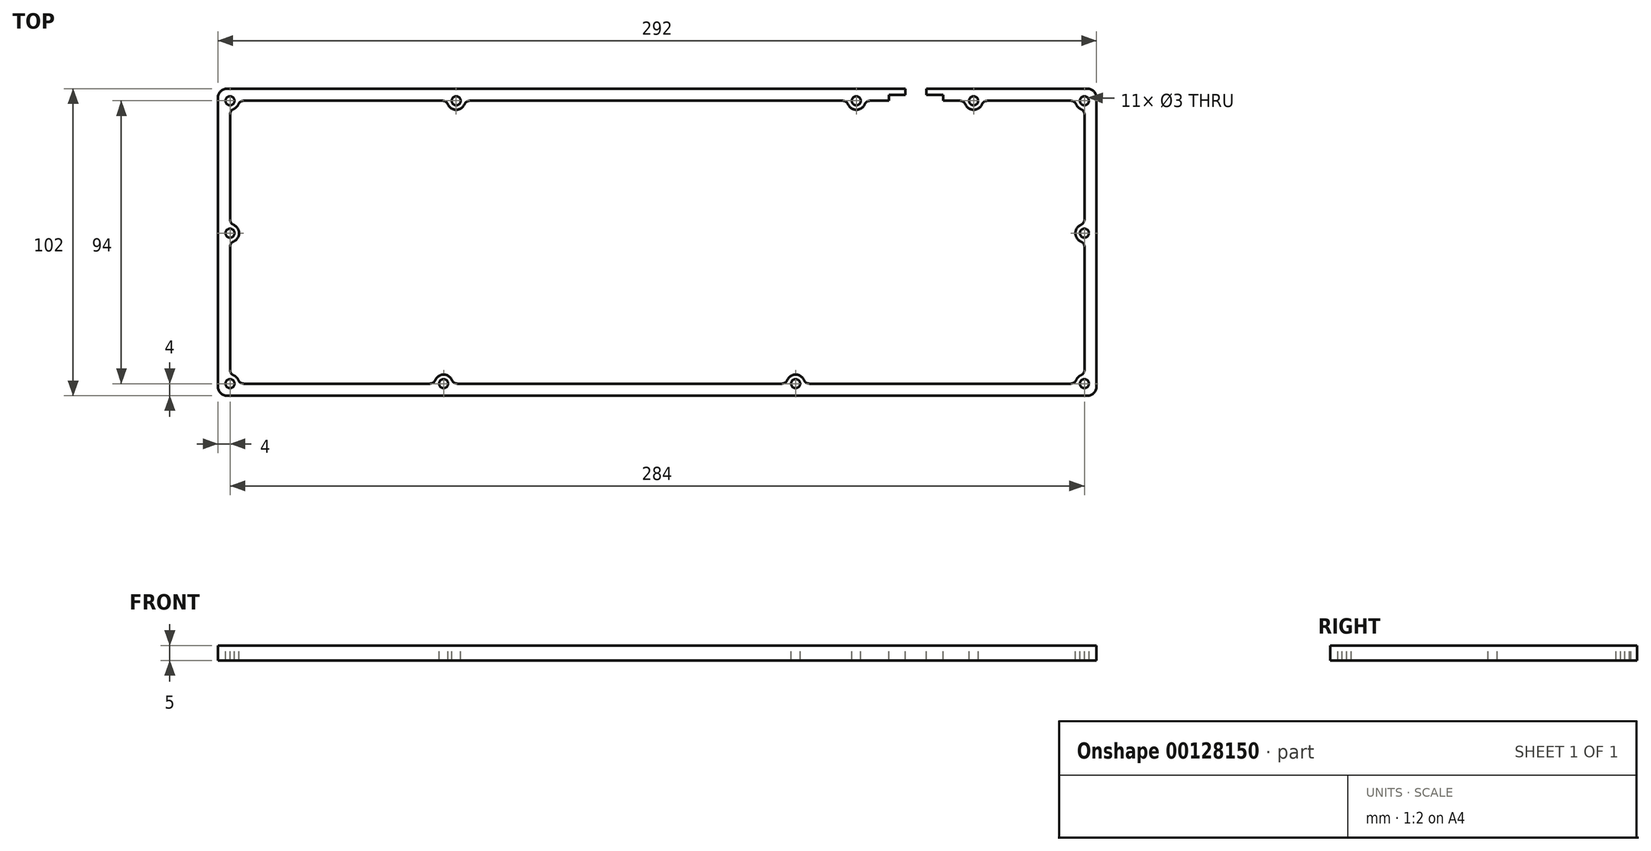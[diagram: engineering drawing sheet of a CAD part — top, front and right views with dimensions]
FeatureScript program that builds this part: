
annotation { "Feature Type Name" : "Feature", "Feature Type Description" : "" }
export const myFeature = defineFeature(function(context is Context, id is Id, definition is map)
    precondition{}
    {
        {
            var Q0;
            Q0=qCreatedBy(makeId("Top.planeOp"),FACE);
            var sketch = newSketch(context, id + "F0", { "sketchPlane" : qUnion([Q0])});
            skLineSegment(sketch, "E0.bottom", {"start": v(143, 51) * mm, "end": v(-143, 51) * mm});
            skLineSegment(sketch, "E0.top", {"start": v(143, -51) * mm, "end": v(-143, -51) * mm});
            skLineSegment(sketch, "E0.left", {"start": v(146, 48) * mm, "end": v(146, -48) * mm});
            skLineSegment(sketch, "E0.right", {"start": v(-146, 48) * mm, "end": v(-146, -48) * mm});
            skPoint(sketch, "E1.visualSharp", {"position": v(-146, 51) * mm});
            skArc(sketch, "E1.filletArc", {"start": v(-143, 51) * mm, "mid": v(-145.12, 50.12) * mm, "end": v(-146, 48) * mm});
            skPoint(sketch, "E2.visualSharp", {"position": v(-146, -51) * mm});
            skArc(sketch, "E2.filletArc", {"start": v(-146, -48) * mm, "mid": v(-145.12, -50.12) * mm, "end": v(-143, -51) * mm});
            skPoint(sketch, "E3.visualSharp", {"position": v(146, -51) * mm});
            skArc(sketch, "E3.filletArc", {"start": v(143, -51) * mm, "mid": v(145.12, -50.12) * mm, "end": v(146, -48) * mm});
            skArc(sketch, "E4.filletArc", {"start": v(146, 48) * mm, "mid": v(145.12, 50.12) * mm, "end": v(143, 51) * mm});
            skSolve(sketch);
        }
        {
            var Q0;
            Q0=qSketchRegion(id+"F0",true);
            extrude(context, id + "F1", {"entities" : qUnion([Q0]), "depth" : 5 * mm});
        }
        {
            var Q0;
            Q0=makeQuery(id+"F1.opExtrude","CAP_FACE",FACE,{"disambiguationData":[OSD([sQuery(id+"F0.wireOp",EDGE,"b1609128-1e4d-4f99-a9c0-d1eb6efb653b"),sQuery(id+"F0.wireOp",EDGE,"f4566b4f-cb64-43fb-b69e-2d4997d02e9e"),sQuery(id+"F0.wireOp",EDGE,"c58de4d6-b1a3-4d1c-92d8-0e596c6fe70e"),sQuery(id+"F0.wireOp",EDGE,"5249d06f-5fa9-4bc2-861d-4cda040d6d12"),sQuery(id+"F0.wireOp",EDGE,"a85e44d5-a424-4784-8d57-3f87bcd3cb1f"),sQuery(id+"F0.wireOp",EDGE,"26f2ad72-3e01-41bb-a775-2f8cfdfabe7d"),sQuery(id+"F0.wireOp",EDGE,"58a866ff-a5cd-410d-a599-dedaca65d45f"),sQuery(id+"F0.wireOp",EDGE,"ffbf0b70-5c72-4423-8b02-8f3d0a3b2328"),sQuery(id+"F0.wireOp",EDGE,"7f67b6f4-1288-461f-aa79-609977e3f21a"),sQuery(id+"F0.wireOp",EDGE,"55541f8a-b999-41dc-948e-6a4feb6e2708"),sQuery(id+"F0.wireOp",EDGE,"6f56692b-9edc-44ed-85e6-53072711c858"),sQuery(id+"F0.wireOp",EDGE,"d64ee7ec-02fb-4461-892d-8620c137c8be"),sQuery(id+"F0.wireOp",EDGE,"a331adab-5858-4e06-9c1d-1ebd579e2d6c"),sQuery(id+"F0.wireOp",EDGE,"872b245d-4d85-40be-bc62-1036af002ab7"),sQuery(id+"F0.wireOp",EDGE,"5f5c10bb-96b1-40b4-bf40-71e8b90fd5b4"),sQuery(id+"F0.wireOp",EDGE,"070c8fee-8489-4fd5-82cc-431f9b446bf5"),sQuery(id+"F0.wireOp",EDGE,"0514bdef-a2e6-47cc-91cb-2d3d024f583d"),sQuery(id+"F0.wireOp",EDGE,"38748b5d-75be-4e41-86c7-7b4e33a636ad"),sQuery(id+"F0.wireOp",EDGE,"ef5fee99-fa31-4ebf-9718-ae6e1dd8c854"),sQuery(id+"F0.wireOp",EDGE,"33aefef2-9a3a-4597-9de5-3f6917e2cb92"),sQuery(id+"F0.wireOp",EDGE,"f576047e-5c30-44eb-8430-c6ba2e10f578"),sQuery(id+"F0.wireOp",EDGE,"5237e12e-b54f-4000-b0ec-e2a188ff4113"),sQuery(id+"F0.wireOp",EDGE,"39a89d85-1c88-4538-9ca2-57a00aa53215"),sQuery(id+"F0.wireOp",EDGE,"1d3d1f3f-65d5-432a-a24c-25425600a27e"),sQuery(id+"F0.wireOp",EDGE,"65133dcd-ba31-495c-9030-11ebdab85244"),sQuery(id+"F0.wireOp",EDGE,"59442c7d-f29c-40c5-8460-04e0c5612805"),sQuery(id+"F0.wireOp",EDGE,"7c508e6d-ace5-438d-ae87-594742bffb03"),sQuery(id+"F0.wireOp",EDGE,"96358abd-ade1-4970-8e96-f48957cb49a9"),sQuery(id+"F0.wireOp",EDGE,"beaf586f-d415-4bcd-bc2c-fe17f6c56d29"),sQuery(id+"F0.wireOp",EDGE,"0b1e909e-c7ab-4355-90a4-b9d381122b20"),sQuery(id+"F0.wireOp",EDGE,"07e25036-969a-447a-8387-7472eab81c53"),sQuery(id+"F0.wireOp",EDGE,"4ac198d4-a843-4e16-ab13-53b4b61c7ec9"),sQuery(id+"F0.wireOp",EDGE,"5899e998-bb7d-4984-919d-5380da3ef46d"),sQuery(id+"F0.wireOp",EDGE,"85bf5025-0c0a-493d-8fd5-15a1002b9e1f"),sQuery(id+"F0.wireOp",EDGE,"433a8b32-5078-4fa2-bccb-dd94966a19e2"),sQuery(id+"F0.wireOp",EDGE,"ca2aed50-1aac-4a88-af60-10e4d26c56ce"),sQuery(id+"F0.wireOp",EDGE,"ad785477-14a5-48c7-ba58-707c46f4f765"),sQuery(id+"F0.wireOp",EDGE,"7e877f2a-03cb-4247-a0d1-3f1f17d45f2e"),sQuery(id+"F0.wireOp",EDGE,"5549e225-b8b0-41a5-a1f6-3a747b09e555"),sQuery(id+"F0.wireOp",EDGE,"7757f798-a692-4454-bd86-5a4d4f9a0c34"),sQuery(id+"F0.wireOp",EDGE,"3016f92a-8452-4434-919c-4a7fc7338035"),sQuery(id+"F0.wireOp",EDGE,"898612aa-0cec-428b-94af-f86252429d12"),sQuery(id+"F0.wireOp",EDGE,"a17dd576-292f-4e6b-9663-d9180f696670"),sQuery(id+"F0.wireOp",EDGE,"cbfd38bd-20b5-4d44-be8c-a17f12e052e0"),sQuery(id+"F0.wireOp",EDGE,"70ab0708-ffdb-4529-bf9e-4018cae3591c"),sQuery(id+"F0.wireOp",EDGE,"f406bcac-c7ef-481d-8174-8bc63e706a56"),sQuery(id+"F0.wireOp",EDGE,"dc331ac5-7670-45e9-89c7-03810e187fe8"),sQuery(id+"F0.wireOp",EDGE,"b3191053-ceed-4c24-bda0-5a50d567a071"),sQuery(id+"F0.wireOp",EDGE,"e110f5b5-6a02-4a34-82cf-196097ccbeb4"),sQuery(id+"F0.wireOp",EDGE,"2b5f7b66-3d2f-406f-a6d7-9a85497eda15"),sQuery(id+"F0.wireOp",EDGE,"76b1751e-cd68-4467-988c-686db3de7683"),sQuery(id+"F0.wireOp",EDGE,"16c5760e-34d5-4e50-8f9d-3caf3d151e1b"),sQuery(id+"F0.wireOp",EDGE,"d295ed9f-bfde-424d-aa21-20497ae6f13c"),sQuery(id+"F0.wireOp",EDGE,"ec12ba42-fae9-4e41-9ad7-bf38757b17f0"),sQuery(id+"F0.wireOp",EDGE,"7436cc0e-6ec4-46fe-a53e-8bd212bcf723"),sQuery(id+"F0.wireOp",EDGE,"0cedb4c9-6a6c-43c2-9996-506471cd3255"),sQuery(id+"F0.wireOp",EDGE,"ec54193d-d4cb-4b1f-86fc-2851957baaba"),sQuery(id+"F0.wireOp",EDGE,"4488f506-9ef2-4267-a6cf-a7b00e78e843"),sQuery(id+"F0.wireOp",EDGE,"372820ab-3034-42cd-b4e6-65ef871f9c40"),sQuery(id+"F0.wireOp",EDGE,"6573e008-ca1a-4dee-91fb-cecced364ef1"),sQuery(id+"F0.wireOp",EDGE,"0ea65bf7-9227-4dbe-9352-82978ca5b32e"),sQuery(id+"F0.wireOp",EDGE,"b1bb12b1-79df-4f2c-a40f-21d0aa567c24"),sQuery(id+"F0.wireOp",EDGE,"0c1536de-d6b0-46e4-9ba7-2841298be202"),sQuery(id+"F0.wireOp",EDGE,"207e1af1-11f0-4a44-9182-2a9f56c0d657"),sQuery(id+"F0.wireOp",EDGE,"27c13fe8-c982-4180-82e1-206dc62b37cb"),sQuery(id+"F0.wireOp",EDGE,"df3f2611-b4d2-4e5e-a9a9-9197ed178f10"),sQuery(id+"F0.wireOp",EDGE,"67ca35e5-e03d-4edf-9133-55c0f28c00dd"),sQuery(id+"F0.wireOp",EDGE,"211b09a9-55cd-462d-ac42-8101b668ed7f"),sQuery(id+"F0.wireOp",EDGE,"3790da84-eb6b-418a-b30a-773cb8711b72"),sQuery(id+"F0.wireOp",EDGE,"8ad775da-4dcc-4f57-b984-0bd12b45c958"),sQuery(id+"F0.wireOp",EDGE,"46f09f23-81b2-4bbc-9572-84064063ea46"),sQuery(id+"F0.wireOp",EDGE,"375117c6-4bbc-4c16-b11f-bde5a02c8ddd"),sQuery(id+"F0.wireOp",EDGE,"edf3fd68-21bd-4dda-b02f-30e2386ebe8c"),sQuery(id+"F0.wireOp",EDGE,"e9b376d0-4e66-4361-894a-f7f99b0a4dba"),sQuery(id+"F0.wireOp",EDGE,"7deef6e9-a95f-4fef-90d6-14df86437aaf"),sQuery(id+"F0.wireOp",EDGE,"3a2c3b9f-72e5-46fb-b22f-c3b3668238e3"),sQuery(id+"F0.wireOp",EDGE,"ef61160d-285f-4999-b3d1-3ad131a5c696"),sQuery(id+"F0.wireOp",EDGE,"5e485a8d-fc2c-447f-9fb7-2a8e8f7db1b8"),sQuery(id+"F0.wireOp",EDGE,"be4b73c1-2188-4d56-b092-b0e9aa332c99"),sQuery(id+"F0.wireOp",EDGE,"7886a41d-8e50-4074-9c4a-38b5df8d299c"),sQuery(id+"F0.wireOp",EDGE,"4e7a6acf-1550-41f7-a348-87a73df4ade2"),sQuery(id+"F0.wireOp",EDGE,"3075fc72-2a9a-4c54-a333-3b9aff6871ba"),sQuery(id+"F0.wireOp",EDGE,"1b470988-ea39-4ef3-b94f-c351ab6970c0"),sQuery(id+"F0.wireOp",EDGE,"d5d0fb32-3312-47e0-b08e-500f4e3a8d6f"),sQuery(id+"F0.wireOp",EDGE,"c95a7a57-a701-41e8-a435-0717771ea27e"),sQuery(id+"F0.wireOp",EDGE,"72f5413f-f806-4961-a1f2-17e8c49a2dbe"),sQuery(id+"F0.wireOp",EDGE,"12295bb0-ec03-4baf-b844-216b01d10c7f"),sQuery(id+"F0.wireOp",EDGE,"ea74abaf-c7a4-4655-a14d-8def43b58c3b"),sQuery(id+"F0.wireOp",EDGE,"fc38e52a-d66c-41f3-a18f-2ab74fc9a3aa"),sQuery(id+"F0.wireOp",EDGE,"b9a872e7-607d-4140-9fac-37e865748f2f"),sQuery(id+"F0.wireOp",EDGE,"469ab4fc-23a3-4a44-8d10-edb1ebb05813"),sQuery(id+"F0.wireOp",EDGE,"6c8f3efd-a16e-4969-a36d-9367de4a04a8"),sQuery(id+"F0.wireOp",EDGE,"d914cece-980e-4aa7-9a19-217e5638b189"),sQuery(id+"F0.wireOp",EDGE,"0d8dcd5d-387b-402a-9c60-ffcbd0bb72cc"),sQuery(id+"F0.wireOp",EDGE,"8cf55217-a1b6-4c1c-9f03-72966d881f0b"),sQuery(id+"F0.wireOp",EDGE,"4053d66f-c8cf-4424-b222-ee203ee23c1e"),sQuery(id+"F0.wireOp",EDGE,"87d9ca37-d664-469b-a4c7-7af1bd52c0ff"),sQuery(id+"F0.wireOp",EDGE,"c0a5d230-8ae8-4271-ac44-5db517de8359"),sQuery(id+"F0.wireOp",EDGE,"1c324c12-bb8f-4aad-bd93-a065141bcc31"),sQuery(id+"F0.wireOp",EDGE,"5157ba3e-39b2-42a3-aeba-34e1f65bc982"),sQuery(id+"F0.wireOp",EDGE,"37ae300f-3520-4053-852e-9cb6712c105c"),sQuery(id+"F0.wireOp",EDGE,"e56d4f24-566a-4093-9c1d-03fa3ce6c3fd"),sQuery(id+"F0.wireOp",EDGE,"c14c5ada-49ad-40e8-9107-312975a1c3f7"),sQuery(id+"F0.wireOp",EDGE,"09f918fb-f6ba-4f35-826c-9be1aaa1e634"),sQuery(id+"F0.wireOp",EDGE,"1a04a7b3-ebb9-45f2-aa82-77a2838be510"),sQuery(id+"F0.wireOp",EDGE,"8b1de847-c452-41c5-811c-5ab6a2f757b0"),sQuery(id+"F0.wireOp",EDGE,"07133ebf-dc20-4f31-a97c-dbe7588edc2e"),sQuery(id+"F0.wireOp",EDGE,"82b11f7f-3426-4d96-a479-9e8199cbbcbe"),sQuery(id+"F0.wireOp",EDGE,"692c3182-390b-47c5-b81b-f7c9554c5188"),sQuery(id+"F0.wireOp",EDGE,"ec9cd909-a83d-4db2-80ed-a48da1c01f2a"),sQuery(id+"F0.wireOp",EDGE,"8999d2ee-b3fd-40a3-91db-70ba8707524c"),sQuery(id+"F0.wireOp",EDGE,"877071da-4e0e-44ee-80f9-18e6a312fe40"),sQuery(id+"F0.wireOp",EDGE,"310de26f-e1f4-4f76-a7a2-31cd6309eb9f"),sQuery(id+"F0.wireOp",EDGE,"ad3c8448-077b-42fa-b66f-cb204dd4b24b"),sQuery(id+"F0.wireOp",EDGE,"dc182899-f22f-43ca-bb7a-d9cff2bb14a0"),sQuery(id+"F0.wireOp",EDGE,"65f270fc-c84c-425a-8765-446292cb4d3e"),sQuery(id+"F0.wireOp",EDGE,"c2b09f90-88b6-4d72-8a72-16f5e25146eb"),sQuery(id+"F0.wireOp",EDGE,"c2295a2a-ded6-4c6f-a2aa-a895bf3941d7"),sQuery(id+"F0.wireOp",EDGE,"c37eb4cb-c588-4c6c-82ac-1d42e178e50a"),sQuery(id+"F0.wireOp",EDGE,"c6fafc2d-4fcb-4607-9bd2-8190c812e452"),sQuery(id+"F0.wireOp",EDGE,"9417043a-912b-430b-98cd-4ce252294d8a"),sQuery(id+"F0.wireOp",EDGE,"25218a79-4e2b-4d76-88a5-5a80dd25db46"),sQuery(id+"F0.wireOp",EDGE,"52fe2f22-f5c3-47de-b85b-7071680885e1"),sQuery(id+"F0.wireOp",EDGE,"8db425a6-9809-493b-a625-842b3707d4f8"),sQuery(id+"F0.wireOp",EDGE,"108efb8e-72e4-46dc-b29e-3530763ab2cb"),sQuery(id+"F0.wireOp",EDGE,"37e6c475-f92b-460d-bb35-4d3434045b59"),sQuery(id+"F0.wireOp",EDGE,"41b95ee3-14c1-4901-89de-568e1f007773"),sQuery(id+"F0.wireOp",EDGE,"01807cc5-b0aa-4840-a249-294bda683d07"),sQuery(id+"F0.wireOp",EDGE,"152e1f9d-8930-4523-a05f-674d844d7707"),sQuery(id+"F0.wireOp",EDGE,"5efd5115-699b-4425-b653-4cc125bcd7d7"),sQuery(id+"F0.wireOp",EDGE,"1cc39329-d833-44ea-a2f6-ea7c9f78653e"),sQuery(id+"F0.wireOp",EDGE,"0dca4560-2abc-4104-80a8-7adf0bc88beb"),sQuery(id+"F0.wireOp",EDGE,"6916323c-6478-4019-a811-1e709e75c72c"),sQuery(id+"F0.wireOp",EDGE,"2451c855-d06f-4170-a402-bb45c563284a"),sQuery(id+"F0.wireOp",EDGE,"8586e523-ca72-4acf-a6f5-917adcdadd36"),sQuery(id+"F0.wireOp",EDGE,"930f09bf-785d-44d0-a635-5104e1f2550d"),sQuery(id+"F0.wireOp",EDGE,"c441b449-73cf-46cf-ad09-9110f26cec35"),sQuery(id+"F0.wireOp",EDGE,"60176a13-c84b-409f-9b5c-2d317961481d"),sQuery(id+"F0.wireOp",EDGE,"fc777e31-b308-4b5e-985b-35cb478bdecb"),sQuery(id+"F0.wireOp",EDGE,"e88cf7bc-e46a-4de7-95e0-dad1476bcc0c"),sQuery(id+"F0.wireOp",EDGE,"96c8cf9e-4ec9-44d1-ad91-7186c6f1f209"),sQuery(id+"F0.wireOp",EDGE,"658329ac-6692-4e40-9ef8-a494bcb0f754"),sQuery(id+"F0.wireOp",EDGE,"d67bae1f-3ffd-4beb-8cc6-29e61c8b342c"),sQuery(id+"F0.wireOp",EDGE,"dbf715f9-25b6-4774-be77-851613eb5e25"),sQuery(id+"F0.wireOp",EDGE,"d8d12f8c-32ed-4466-a5bc-cbc1cfba4feb"),sQuery(id+"F0.wireOp",EDGE,"4beba3b0-c51b-4a43-948d-e7233947d5dc"),sQuery(id+"F0.wireOp",EDGE,"fcfcb946-a851-45fe-a21c-e3f885e48000"),sQuery(id+"F0.wireOp",EDGE,"4d44fab2-dba1-4fbc-848d-77cfe8fac08b"),sQuery(id+"F0.wireOp",EDGE,"5776a788-e3c3-4dac-aeb6-7777a672858e"),sQuery(id+"F0.wireOp",EDGE,"cedf499e-2994-4c9b-b766-b127bb67c415"),sQuery(id+"F0.wireOp",EDGE,"0a2e2db6-b390-46fd-b74c-53757edf0af6"),sQuery(id+"F0.wireOp",EDGE,"4ce94d68-acc0-4cfe-bd55-ec03fe200a5b"),sQuery(id+"F0.wireOp",EDGE,"e0c07793-b957-4333-96dc-a294f1e2ceb0"),sQuery(id+"F0.wireOp",EDGE,"41979a11-f1a0-4749-a17a-603b7864cc01"),sQuery(id+"F0.wireOp",EDGE,"aa3ca26f-036c-439d-b566-5430048ebdf9"),sQuery(id+"F0.wireOp",EDGE,"249b810b-8968-482f-8bbc-e4399ea1180f"),sQuery(id+"F0.wireOp",EDGE,"3f1de34e-7a13-4160-8f1e-59d99b5a4c3a"),sQuery(id+"F0.wireOp",EDGE,"f0e1049c-435a-4f02-948e-5f98f668222f"),sQuery(id+"F0.wireOp",EDGE,"dceacdf6-e703-4809-b70b-d17cfe04b7d7"),sQuery(id+"F0.wireOp",EDGE,"bdd4c6ec-239a-424d-8041-67786f5d4ce7"),sQuery(id+"F0.wireOp",EDGE,"44e7c303-723b-4c42-a54a-8f557ff9a9f6"),sQuery(id+"F0.wireOp",EDGE,"e59f6ee7-3ba8-4e2b-b5d6-6e605825de7d"),sQuery(id+"F0.wireOp",EDGE,"3867d971-9346-4093-a9b2-274161278cdc"),sQuery(id+"F0.wireOp",EDGE,"d52ba1ae-d7a3-467c-9b67-1ae8c09bf28e"),sQuery(id+"F0.wireOp",EDGE,"1800a961-f957-4766-bec1-88f23ee5c048"),sQuery(id+"F0.wireOp",EDGE,"944022d4-31d1-4345-9843-0181748df1e1"),sQuery(id+"F0.wireOp",EDGE,"56ca7d79-5fc4-42fd-843a-33c232b6b3c3"),sQuery(id+"F0.wireOp",EDGE,"098c2286-8095-4fed-8dd0-5a8dec876cb3"),sQuery(id+"F0.wireOp",EDGE,"2ad36734-b040-4264-b8f6-ee2da5387eb9"),sQuery(id+"F0.wireOp",EDGE,"ccc487cc-2c29-4e42-a366-3ba57780b9a2"),sQuery(id+"F0.wireOp",EDGE,"7b328234-d38a-4842-b15d-1fbe1fd70208"),sQuery(id+"F0.wireOp",EDGE,"3732f762-4107-4d06-83e4-c8630a2c37fb"),sQuery(id+"F0.wireOp",EDGE,"8b64106c-834e-4e21-a7c0-f3940f540fb2"),sQuery(id+"F0.wireOp",EDGE,"6e7361da-996f-46b3-a434-00db9b4c9c9f"),sQuery(id+"F0.wireOp",EDGE,"b0b43ae6-5ac0-41e1-a04e-e485c33c99f8"),sQuery(id+"F0.wireOp",EDGE,"db5e65e6-5182-4048-9572-11a43cb11c51"),sQuery(id+"F0.wireOp",EDGE,"26e7e85a-b403-48fa-8c29-07448647ad8f"),sQuery(id+"F0.wireOp",EDGE,"515b21e0-8220-4d96-96a0-4c14be87b64b"),sQuery(id+"F0.wireOp",EDGE,"aa12bfdd-f8d8-4067-91a8-122e35d45f26"),sQuery(id+"F0.wireOp",EDGE,"9aa84255-1989-40c3-bf0d-31009647c77f"),sQuery(id+"F0.wireOp",EDGE,"aa9638c1-c68d-45f6-940c-d0f327c0fa45"),sQuery(id+"F0.wireOp",EDGE,"251b7c26-2c5b-48f1-8bde-e20a856a34ff"),sQuery(id+"F0.wireOp",EDGE,"18e7e5a9-24b2-485b-ab29-6ec4d7284516"),sQuery(id+"F0.wireOp",EDGE,"f4cd6263-1ac9-4123-a1aa-8b6f3d1fe724"),sQuery(id+"F0.wireOp",EDGE,"34207eab-8dad-445e-ac2c-5e7baad48e02"),sQuery(id+"F0.wireOp",EDGE,"d2cd9a5c-99c8-49cb-9122-6c3893475af4"),sQuery(id+"F0.wireOp",EDGE,"0ab99930-a22d-41a5-8d7a-f072e43d683d"),sQuery(id+"F0.wireOp",EDGE,"ba1f877b-ae2d-41b0-a78f-99f645971353"),sQuery(id+"F0.wireOp",EDGE,"7655611b-0d56-496a-9af6-17078dfc8983"),sQuery(id+"F0.wireOp",EDGE,"2217c71d-48f5-44f0-b6aa-e70c41dec14e"),sQuery(id+"F0.wireOp",EDGE,"2da62ed5-bda3-4005-8c82-b2de019464e8"),sQuery(id+"F0.wireOp",EDGE,"b9e5db85-9e65-4104-9569-ca807059eb4d"),sQuery(id+"F0.wireOp",EDGE,"e8855f58-9b24-4e18-bc1c-a0daeed810ba"),sQuery(id+"F0.wireOp",EDGE,"6c73f8f0-d719-4729-89df-4c554db3bf8c"),sQuery(id+"F0.wireOp",EDGE,"99502265-d697-4b9c-a12a-a7646a77523d"),sQuery(id+"F0.wireOp",EDGE,"5ad33bb7-7d8c-4f73-a2bd-749fa85a955e"),sQuery(id+"F0.wireOp",EDGE,"ffa3529a-edc2-4b05-9642-06e0e9a42b66"),sQuery(id+"F0.wireOp",EDGE,"221bf0c5-454d-44e2-b718-00ef1a2cf6b4"),sQuery(id+"F0.wireOp",EDGE,"2bf5e5ca-39b4-4044-8377-129965e258c5"),sQuery(id+"F0.wireOp",EDGE,"ba879806-eb56-4bd7-bf01-18ec1c857bc0"),sQuery(id+"F0.wireOp",EDGE,"64b71d1f-be08-4438-bafa-bb0b385583c3"),sQuery(id+"F0.wireOp",EDGE,"9a261f28-0ea3-4c64-a250-fe02b8de4198"),sQuery(id+"F0.wireOp",EDGE,"9c6a15b5-d89c-4f27-9035-4432c0c29f03"),sQuery(id+"F0.wireOp",EDGE,"39fc6f70-527d-491a-b3cc-87afca1fd921"),sQuery(id+"F0.wireOp",EDGE,"83ff7e70-d247-44e0-9e1a-45f528f1984e"),sQuery(id+"F0.wireOp",EDGE,"8c19abdc-fab5-49c6-a1e3-3ac5321561f2"),sQuery(id+"F0.wireOp",EDGE,"38f5175e-ca97-4091-a899-2fc862d9fcf7"),sQuery(id+"F0.wireOp",EDGE,"a6b59a2b-11a6-4381-9ec9-9e4786140b61"),sQuery(id+"F0.wireOp",EDGE,"a6aa3d57-10a3-484e-8f69-3d26024ead90"),sQuery(id+"F0.wireOp",EDGE,"cab9f132-7f02-4cf2-a837-44b314ab0f2d"),sQuery(id+"F0.wireOp",EDGE,"4d87c6e3-345b-4698-85be-4c1066c996ba"),sQuery(id+"F0.wireOp",EDGE,"100f6826-a35e-44dc-8f5e-91e6494c0734"),sQuery(id+"F0.wireOp",EDGE,"6b51b95a-e805-4a4c-b3ce-42549b1f7c4f"),sQuery(id+"F0.wireOp",EDGE,"4974438e-2757-4174-b66e-648bb066325b"),sQuery(id+"F0.wireOp",EDGE,"06557fa0-7690-4017-ac39-cec9dddb7ac3"),sQuery(id+"F0.wireOp",EDGE,"190d5702-5898-49b5-8b03-446313d35a85"),sQuery(id+"F0.wireOp",EDGE,"13d402cf-df92-4d9a-ac9d-1f67946c0a84"),sQuery(id+"F0.wireOp",EDGE,"2f2b7a4a-fe61-4bf2-9a19-afa51de3c721"),sQuery(id+"F0.wireOp",EDGE,"89631652-7db3-4c6b-99e7-db613ff7bbbb"),sQuery(id+"F0.wireOp",EDGE,"9bb81fc8-ca7b-4002-871d-2f89aed8432f"),sQuery(id+"F0.wireOp",EDGE,"a13c4922-8a72-4012-be87-7b5d4d768a52"),sQuery(id+"F0.wireOp",EDGE,"2badb0fd-de87-488b-8ff2-1cf5654be30e"),sQuery(id+"F0.wireOp",EDGE,"3885baab-ef1d-4d35-a85f-7a32c066c2bb"),sQuery(id+"F0.wireOp",EDGE,"5dec05d8-971c-49fe-8ee5-de689f2777ed"),sQuery(id+"F0.wireOp",EDGE,"4173ea56-7147-43d2-9c71-5769336bf9f5"),sQuery(id+"F0.wireOp",EDGE,"ac75d90e-cfd8-4d37-ba29-49a000d3f1ae"),sQuery(id+"F0.wireOp",EDGE,"98559af5-3831-4093-9a27-000fd7a0f36c"),sQuery(id+"F0.wireOp",EDGE,"e31d4e9e-ec26-4480-9e00-58e09570ae7e"),sQuery(id+"F0.wireOp",EDGE,"e82aada4-95ef-49cd-9523-bf5d0496c439"),sQuery(id+"F0.wireOp",EDGE,"21f6afce-f90f-4921-86bd-c08a04096671"),sQuery(id+"F0.wireOp",EDGE,"3c7f96f7-af1a-4bca-82d7-7f24edd57999"),sQuery(id+"F0.wireOp",EDGE,"9c442e46-f741-49c2-ae82-587b697e79f8"),sQuery(id+"F0.wireOp",EDGE,"f57068b1-2418-4c58-9872-b1a6e01bfd01"),sQuery(id+"F0.wireOp",EDGE,"aca98637-d3dc-411b-a35d-96c25150bc33"),sQuery(id+"F0.wireOp",EDGE,"d832a37b-e081-415c-bcce-cbaaf2c07a6e"),sQuery(id+"F0.wireOp",EDGE,"c9b6084d-535c-4eea-879b-8436754e0a02"),sQuery(id+"F0.wireOp",EDGE,"83c218aa-2010-4a7a-b09b-f6f7594d2848"),sQuery(id+"F0.wireOp",EDGE,"25d1440d-df07-499d-9911-16ffe4e38f84"),sQuery(id+"F0.wireOp",EDGE,"b6ddaadb-7141-4236-b186-f6da43c88cd6"),sQuery(id+"F0.wireOp",EDGE,"31b5fb8c-a189-40bf-8a18-47b0cc85132f"),sQuery(id+"F0.wireOp",EDGE,"37fcbbbc-e4b3-40ea-a50b-883800e78a5e"),sQuery(id+"F0.wireOp",EDGE,"d3f70543-5bb9-47e1-870b-7f1758817613"),sQuery(id+"F0.wireOp",EDGE,"f9c8d4e8-c029-4b82-b080-4960ce172a88"),sQuery(id+"F0.wireOp",EDGE,"39afe83d-89d6-44e1-8ada-1b9ab1a1485e"),sQuery(id+"F0.wireOp",EDGE,"a4da8c96-5464-43a0-a877-97641311b988"),sQuery(id+"F0.wireOp",EDGE,"501f0886-9544-46dc-adfd-6bdb9374b70b"),sQuery(id+"F0.wireOp",EDGE,"a040e1e7-e6a2-42d4-8a0a-b58d54095c78"),sQuery(id+"F0.wireOp",EDGE,"266685c9-b8b4-4f14-8dcb-010c88eb1083"),sQuery(id+"F0.wireOp",EDGE,"a78f4bb4-8cf1-45b3-bd54-ed21ce6b7e77"),sQuery(id+"F0.wireOp",EDGE,"9fed2e65-49e2-48d5-91fd-bef8366991b9"),sQuery(id+"F0.wireOp",EDGE,"e5b929db-a2ea-4433-8172-c9d0a43971ef"),sQuery(id+"F0.wireOp",EDGE,"d15be14e-e4f7-4dc7-82c5-c08f03b6a96b"),sQuery(id+"F0.wireOp",EDGE,"4e03f35e-05bc-4b6a-8889-a9f08c83d29e"),sQuery(id+"F0.wireOp",EDGE,"d6bfbf06-55c8-4808-983c-7f728cc75ab0"),sQuery(id+"F0.wireOp",EDGE,"625082b8-4dc8-485c-a11f-6dd84b90f705"),sQuery(id+"F0.wireOp",EDGE,"6e6ef2d8-6f26-4221-b3c2-0aed2e8eeeea"),sQuery(id+"F0.wireOp",EDGE,"fde2ada2-eb67-4ef0-beec-9eb2ee9529bd"),sQuery(id+"F0.wireOp",EDGE,"ff846ca3-1931-47eb-b30c-d282e952b59a"),sQuery(id+"F0.wireOp",EDGE,"2f7f04d9-0a77-41a9-a710-5b10e0b304b1"),sQuery(id+"F0.wireOp",EDGE,"7ec9521f-18ef-41a3-8966-0f2aee6ff685"),sQuery(id+"F0.wireOp",EDGE,"b32b4623-d4c6-405e-ac90-b876da4664bc"),sQuery(id+"F0.wireOp",EDGE,"e1e232c8-27d0-46d2-b10c-53b0933a74ee"),sQuery(id+"F0.wireOp",EDGE,"4dc7a203-5312-4640-a274-b1f682c48a83"),sQuery(id+"F0.wireOp",EDGE,"5ec18aa4-844b-4fd6-bb0f-ea66bd33227a"),sQuery(id+"F0.wireOp",EDGE,"82f6a369-effc-4e42-8078-1b4068fc9ca4"),sQuery(id+"F0.wireOp",EDGE,"1d6cbc2a-f3a5-4e8c-9653-84e9777b349f"),sQuery(id+"F0.wireOp",EDGE,"394b4bd7-1cda-4ff6-a125-fc6477bc39fb"),sQuery(id+"F0.wireOp",EDGE,"57d5dcee-28cf-4cba-8a40-e39ca4d8f1a1"),sQuery(id+"F0.wireOp",EDGE,"dc2c0885-5591-4e00-be3a-884cbec6d151"),sQuery(id+"F0.wireOp",EDGE,"aad2d9a4-5522-4183-a005-46352570c096"),sQuery(id+"F0.wireOp",EDGE,"ab95f565-e86b-404d-b46e-959ec70fe326"),sQuery(id+"F0.wireOp",EDGE,"1a3e4d60-116d-4e15-acde-dbb54cdc3e9f"),sQuery(id+"F0.wireOp",EDGE,"2f20cbd4-76e3-4f74-8986-d968588fc4e8"),sQuery(id+"F0.wireOp",EDGE,"753a2c14-8ac4-46b1-adcd-2c7270b5770b"),sQuery(id+"F0.wireOp",EDGE,"6aad7a9e-0483-4a9a-9044-6663aff9a316"),sQuery(id+"F0.wireOp",EDGE,"0a2596d7-6d10-47f5-a9f2-89b9bf7a1f87"),sQuery(id+"F0.wireOp",EDGE,"85a143d8-6ea7-4fbd-94c9-d270f6c85c66"),sQuery(id+"F0.wireOp",EDGE,"8d7e53f5-cfe5-40a6-8ffa-4bf0b95a127d"),sQuery(id+"F0.wireOp",EDGE,"3fd28192-c398-4a49-a92d-335951c4506c"),sQuery(id+"F0.wireOp",EDGE,"17979889-b5c4-4d1c-9b8a-43c43d671ab6"),sQuery(id+"F0.wireOp",EDGE,"92f33dad-6f90-4d6e-b4ec-202fb2800c95"),sQuery(id+"F0.wireOp",EDGE,"0ab45290-3409-407a-97d1-1798937913bc"),sQuery(id+"F0.wireOp",EDGE,"2c5f605b-9cbf-444f-b4f0-d3661b8886fe"),sQuery(id+"F0.wireOp",EDGE,"b840f495-8230-455c-8c8f-9fcbc6fdd650"),sQuery(id+"F0.wireOp",EDGE,"9ef30627-d4f6-40fe-a0c9-13aa0f7e93fc"),sQuery(id+"F0.wireOp",EDGE,"4461d5c2-7a67-47f2-8962-6c99b4a5204c"),sQuery(id+"F0.wireOp",EDGE,"081d79c5-aad2-40dd-bb6e-7a0aabafd1b6"),sQuery(id+"F0.wireOp",EDGE,"f9e75d03-768d-470f-8f10-b6e003a855e7"),sQuery(id+"F0.wireOp",EDGE,"4c0c9c3d-329b-4999-a02d-13464766462d"),sQuery(id+"F0.wireOp",EDGE,"7b7e0f44-dbb4-4f47-be36-2e83010483bd"),sQuery(id+"F0.wireOp",EDGE,"1e10e814-c332-4ecf-91b1-3ebca5584570"),sQuery(id+"F0.wireOp",EDGE,"59ac1f3f-6679-4629-b80b-61bd17a2b2f8"),sQuery(id+"F0.wireOp",EDGE,"ae25387f-1f81-4d49-9314-d22d11f38b5d"),sQuery(id+"F0.wireOp",EDGE,"305fb3d6-1341-4639-b3e8-1374f76d0736"),sQuery(id+"F0.wireOp",EDGE,"8d6a009a-bdc3-4505-b116-9dfb21e65cd5"),sQuery(id+"F0.wireOp",EDGE,"e117250e-32e6-4a26-86f8-0e13f4d16bec"),sQuery(id+"F0.wireOp",EDGE,"41386a07-9f86-4093-b2d2-7aa4842ce662"),sQuery(id+"F0.wireOp",EDGE,"9c5f58e5-8954-465d-9504-48b7d980ba6b"),sQuery(id+"F0.wireOp",EDGE,"56670a70-7e0d-4b80-9dd5-68985d74d020"),sQuery(id+"F0.wireOp",EDGE,"8ce40b0d-489f-4ffc-a366-aa5d5dbd9682"),sQuery(id+"F0.wireOp",EDGE,"9cafe44c-6f76-40ea-9fd8-f282bb15773c"),sQuery(id+"F0.wireOp",EDGE,"a5e7a8d2-c55f-494a-9a49-f046675af114"),sQuery(id+"F0.wireOp",EDGE,"1bec7831-0536-4ac3-afc2-476294aa08ed"),sQuery(id+"F0.wireOp",EDGE,"fa5222d6-37b7-4824-9e79-5f0c5d09a009"),sQuery(id+"F0.wireOp",EDGE,"b3891244-9859-4daf-be27-380808788fd3"),sQuery(id+"F0.wireOp",EDGE,"c7feb413-078f-49a4-85ea-459ed2746111"),sQuery(id+"F0.wireOp",EDGE,"b0081492-be99-4dc3-b230-7d0aab91f03c"),sQuery(id+"F0.wireOp",EDGE,"7edeb0e6-a732-4e48-a81b-608c459c7c27"),sQuery(id+"F0.wireOp",EDGE,"867c9e95-7424-4e1d-87d8-b22a68c3c025"),sQuery(id+"F0.wireOp",EDGE,"9c27c829-7a0d-4637-b876-c453130a447f"),sQuery(id+"F0.wireOp",EDGE,"d3c4b1f1-9457-4f91-b126-2c4e7d60c85a"),sQuery(id+"F0.wireOp",EDGE,"22a6e6f7-cc3c-41fb-9e90-cc46def12613"),sQuery(id+"F0.wireOp",EDGE,"83a76977-9a06-423b-ae66-cd00626cf560"),sQuery(id+"F0.wireOp",EDGE,"3f29e2a1-a5c9-4722-b659-4ee6781ed382"),sQuery(id+"F0.wireOp",EDGE,"fd5f3ce2-0948-486b-aa29-b785551bf386"),sQuery(id+"F0.wireOp",EDGE,"7599906f-92b1-4219-8dd3-bf5d8a31e626"),sQuery(id+"F0.wireOp",EDGE,"2add90be-772b-4aa5-b982-7332210cce71"),sQuery(id+"F0.wireOp",EDGE,"2a6877ed-6dab-4773-a72d-47a1a77d2c9f"),sQuery(id+"F0.wireOp",EDGE,"4cbb10b3-3aa2-4e86-8ee4-578b1c38922a"),sQuery(id+"F0.wireOp",EDGE,"ffd5fb1b-367a-48dc-84a3-11640e968880"),sQuery(id+"F0.wireOp",EDGE,"b6fbc371-c7be-499f-aee2-95a98a174042"),sQuery(id+"F0.wireOp",EDGE,"412ed036-02e6-436f-ba39-a533e7d8d566"),sQuery(id+"F0.wireOp",EDGE,"c40d6e9d-23c6-4394-82e4-2dcbbd49f451"),sQuery(id+"F0.wireOp",EDGE,"57b9e075-483a-4aa5-9f8d-aed7ae9a4015"),sQuery(id+"F0.wireOp",EDGE,"7a8d3c14-78e7-4489-a911-4a74efbfc4b3"),sQuery(id+"F0.wireOp",EDGE,"09ad2b53-dbf9-4d92-8b7e-6870fa5a446d"),sQuery(id+"F0.wireOp",EDGE,"1f6abc6c-9e44-49fd-bf99-f16bc5950d3f"),sQuery(id+"F0.wireOp",EDGE,"f41b703e-44d6-4482-948b-e04385fb91a8"),sQuery(id+"F0.wireOp",EDGE,"91d70adb-115e-4ffb-a395-2b6cacca741c"),sQuery(id+"F0.wireOp",EDGE,"dda57363-ed32-4561-a2c0-083cdafd8a37"),sQuery(id+"F0.wireOp",EDGE,"7a3fefc2-0a72-4021-b326-2823abfe09e3"),sQuery(id+"F0.wireOp",EDGE,"4b5e01bc-3fbf-4abe-aed3-b0d3e09be2f4"),sQuery(id+"F0.wireOp",EDGE,"0a378d94-3c4a-453d-92a8-3da6627ba44f"),sQuery(id+"F0.wireOp",EDGE,"96939f80-8f1b-456a-a56f-a45e4b84fff2"),sQuery(id+"F0.wireOp",EDGE,"8690dbd8-32d0-4c24-9a6f-21ccdc6d1b7b"),sQuery(id+"F0.wireOp",EDGE,"41a9296a-9171-4399-88f5-af94295a5342"),sQuery(id+"F0.wireOp",EDGE,"de1af690-d43f-4b9a-858b-9be29a448911"),sQuery(id+"F0.wireOp",EDGE,"edbdedd4-bb9a-406e-9dd7-aaae3bf236ae"),sQuery(id+"F0.wireOp",EDGE,"d51c5f01-75a1-4b6c-a957-fca7eef8146b"),sQuery(id+"F0.wireOp",EDGE,"b3fd92ac-78b6-41b1-afc0-ee29ddcca53f"),sQuery(id+"F0.wireOp",EDGE,"2cda1eef-ec72-41ac-bce3-61a85240fdd5"),sQuery(id+"F0.wireOp",EDGE,"71c48189-8c54-4eb2-a12e-6105fa345c64"),sQuery(id+"F0.wireOp",EDGE,"9f1062f6-9304-4d8d-9ce9-abb74b2d722e"),sQuery(id+"F0.wireOp",EDGE,"bf896698-4176-4980-b20a-78c865a3d341"),sQuery(id+"F0.wireOp",EDGE,"b7b6dc4d-cf79-4355-b5e9-8fde5f500ec0"),sQuery(id+"F0.wireOp",EDGE,"7f73ae36-54b1-49d6-8841-5560dfb65061"),sQuery(id+"F0.wireOp",EDGE,"62dbb698-6cc5-4ac8-9783-cd1c26481057"),sQuery(id+"F0.wireOp",EDGE,"a9b6f9ac-2563-4c2d-9a9e-898be4e77e27"),sQuery(id+"F0.wireOp",EDGE,"b748b83c-cc52-469c-b6c0-f44465017a8c"),sQuery(id+"F0.wireOp",EDGE,"c8facb2b-b026-4934-a63b-b5607b87cb66"),sQuery(id+"F0.wireOp",EDGE,"cfe49408-1198-43da-bc37-20620b43ecba"),sQuery(id+"F0.wireOp",EDGE,"c7d4460d-85fc-4d6f-b61a-7110802d6a6a"),sQuery(id+"F0.wireOp",EDGE,"1b071a63-40b8-4c94-9dfb-8e2c33fe026c"),sQuery(id+"F0.wireOp",EDGE,"5085e82c-c506-464d-9a31-33060296f019"),sQuery(id+"F0.wireOp",EDGE,"f39580b1-4943-4daa-9aeb-e63f821f6646"),sQuery(id+"F0.wireOp",EDGE,"faafab1b-27c7-4fec-a70a-5a6f0e2d9a62"),sQuery(id+"F0.wireOp",EDGE,"db622875-df72-4ad8-b8c4-500b0e330896"),sQuery(id+"F0.wireOp",EDGE,"680b1a25-a5b3-435f-962b-75b95a27b20f"),sQuery(id+"F0.wireOp",EDGE,"9615cfa5-d949-43e5-b88d-47ba86214343"),sQuery(id+"F0.wireOp",EDGE,"c9b12d91-4184-4bdc-82a4-c7504ad794e0"),sQuery(id+"F0.wireOp",EDGE,"856246d2-e0bf-4f01-aded-4de051bcbc94"),sQuery(id+"F0.wireOp",EDGE,"f6dddd8d-1894-43b6-a926-3e2663eaabd2"),sQuery(id+"F0.wireOp",EDGE,"b1722177-dd49-41cd-ad15-c1adc430affd"),sQuery(id+"F0.wireOp",EDGE,"efb29aa0-0f38-401f-89a6-a67a7e04fdcb"),sQuery(id+"F0.wireOp",EDGE,"681c5269-f780-41cb-9872-6f5a5ac3c074"),sQuery(id+"F0.wireOp",EDGE,"e9f3e534-2fe3-4adf-b3b3-a70aa0e0abbc"),sQuery(id+"F0.wireOp",EDGE,"184a51fd-37f7-4e2e-8b20-b78d3d228c3e"),sQuery(id+"F0.wireOp",EDGE,"c8e7bc03-7667-4963-ac8a-0e4c5ad09257"),sQuery(id+"F0.wireOp",EDGE,"2684f396-274b-4407-9748-250128256beb"),sQuery(id+"F0.wireOp",EDGE,"cb26cbe6-b294-4172-807b-7e2fe063b7af"),sQuery(id+"F0.wireOp",EDGE,"373a3cfd-3014-4e28-9adb-c235d9bd59d7"),sQuery(id+"F0.wireOp",EDGE,"faf1a0ad-00b5-4abd-ba04-7585af7e1ba0"),sQuery(id+"F0.wireOp",EDGE,"E0.bottom"),sQuery(id+"F0.wireOp",EDGE,"E0.top"),sQuery(id+"F0.wireOp",EDGE,"E0.left"),sQuery(id+"F0.wireOp",EDGE,"E0.right")])],"isStart":false});
            var sketch = newSketch(context, id + "F2", { "sketchPlane" : qUnion([Q0])});
            skCircle(sketch, "E5", {"center": v(-142, 47) * mm, "radius": 1.1 * mm});
            skCircle(sketch, "E6", {"center": v(142, 47) * mm, "radius": 1.1 * mm});
            skCircle(sketch, "E7", {"center": v(-66.83, 47) * mm, "radius": 1.1 * mm});
            skCircle(sketch, "E8", {"center": v(66.17, 47) * mm, "radius": 1.1 * mm});
            skCircle(sketch, "E9", {"center": v(-142, -47) * mm, "radius": 1.1 * mm});
            skCircle(sketch, "E10", {"center": v(142, -47) * mm, "radius": 1.1 * mm});
            skCircle(sketch, "E11", {"center": v(-71, -47) * mm, "radius": 1.1 * mm});
            skCircle(sketch, "E12", {"center": v(46, -47) * mm, "radius": 1.1 * mm});
            skCircle(sketch, "E13", {"center": v(142, 3) * mm, "radius": 1.1 * mm});
            skCircle(sketch, "E14", {"center": v(-142, 3) * mm, "radius": 1.1 * mm});
            skSolve(sketch);
        }
        {
            var Q0;
            Q0=qSketchRegion(id+"F2",true);
            extrude(context, id + "F3", {"entities" : qUnion([Q0]), "operationType" : NewBodyOperationType.REMOVE, "endBound" : BoundingType.THROUGH_ALL, "oppositeDirection" : true, "depth" : 25 * mm});
        }
        {
            var Q0;
            Q0=makeQuery(id+"F1.opExtrude","CAP_FACE",FACE,{"disambiguationData":[OSD([sQuery(id+"F0.wireOp",EDGE,"E0.bottom"),sQuery(id+"F0.wireOp",EDGE,"E0.top"),sQuery(id+"F0.wireOp",EDGE,"E0.left"),sQuery(id+"F0.wireOp",EDGE,"E0.right"),sQuery(id+"F0.wireOp",EDGE,"E1.filletArc"),sQuery(id+"F0.wireOp",EDGE,"E2.filletArc"),sQuery(id+"F0.wireOp",EDGE,"E3.filletArc"),sQuery(id+"F0.wireOp",EDGE,"E4.filletArc")])],"isStart":false});
            var sketch = newSketch(context, id + "F4", { "sketchPlane" : qUnion([Q0])});
            skLineSegment(sketch, "E15.top", {"start": v(-137.42, 47) * mm, "end": v(-71.4, 47) * mm});
            skLineSegment(sketch, "E15.right", {"start": v(142, -42.42) * mm, "end": v(142, -1.58) * mm});
            skPoint(sketch, "E15.middle", {"position": v(0, 0) * mm});
            skArc(sketch, "E16", {"start": v(-140.8, 44.25) * mm, "mid": v(-139.88, 44.88) * mm, "end": v(-139.25, 45.8) * mm});
            skArc(sketch, "E17", {"start": v(-69.57, 45.8) * mm, "mid": v(-66.83, 44) * mm, "end": v(-64.08, 45.8) * mm});
            skArc(sketch, "E18", {"start": v(-140.8, 0.25) * mm, "mid": v(-139, 3) * mm, "end": v(-140.8, 5.75) * mm});
            skArc(sketch, "E19", {"start": v(-139.25, -45.8) * mm, "mid": v(-139.88, -44.88) * mm, "end": v(-140.8, -44.25) * mm});
            skArc(sketch, "E20", {"start": v(-68.25, -45.8) * mm, "mid": v(-71, -44) * mm, "end": v(-73.75, -45.8) * mm});
            skArc(sketch, "E21", {"start": v(63.43, 45.8) * mm, "mid": v(66.17, 44) * mm, "end": v(68.92, 45.8) * mm});
            skArc(sketch, "E22", {"start": v(48.75, -45.8) * mm, "mid": v(46, -44) * mm, "end": v(43.25, -45.8) * mm});
            skArc(sketch, "E23", {"start": v(139.25, 45.8) * mm, "mid": v(139.88, 44.88) * mm, "end": v(140.8, 44.25) * mm});
            skArc(sketch, "E24", {"start": v(140.8, -44.25) * mm, "mid": v(139.88, -44.88) * mm, "end": v(139.25, -45.8) * mm});
            skCircle(sketch, "E25", {"center": v(-142, 47) * mm, "radius": 1.5 * mm});
            skCircle(sketch, "E26", {"center": v(-66.83, 47) * mm, "radius": 1.5 * mm});
            skCircle(sketch, "E27", {"center": v(-142, 3) * mm, "radius": 1.5 * mm});
            skCircle(sketch, "E28", {"center": v(-142, -47) * mm, "radius": 1.5 * mm});
            skCircle(sketch, "E29", {"center": v(66.17, 47) * mm, "radius": 1.5 * mm});
            skCircle(sketch, "E30", {"center": v(142, 3) * mm, "radius": 1.5 * mm});
            skCircle(sketch, "E31", {"center": v(142, -47) * mm, "radius": 1.5 * mm});
            skCircle(sketch, "E32", {"center": v(46, -47) * mm, "radius": 1.5 * mm});
            skCircle(sketch, "E33", {"center": v(-71, -47) * mm, "radius": 1.5 * mm});
            skCircle(sketch, "E34", {"center": v(142, 47) * mm, "radius": 1.5 * mm});
            skArc(sketch, "E35", {"start": v(140.8, 5.75) * mm, "mid": v(139, 3) * mm, "end": v(140.8, 0.25) * mm});
            skLineSegment(sketch, "E36.trimOffspring", {"start": v(-62.24, 47) * mm, "end": v(61.6, 47) * mm});
            skLineSegment(sketch, "E37.trimOffspring", {"start": v(70.76, 47) * mm, "end": v(100.6, 47) * mm});
            skLineSegment(sketch, "E38.trimOffspring", {"start": v(142, 7.58) * mm, "end": v(142, 42.42) * mm});
            skLineSegment(sketch, "E39.trimOffspring", {"start": v(50.58, -47) * mm, "end": v(137.42, -47) * mm});
            skLineSegment(sketch, "E40.trimOffspring", {"start": v(-66.42, -47) * mm, "end": v(41.42, -47) * mm});
            skLineSegment(sketch, "E41.trimOffspring", {"start": v(-142, -42.42) * mm, "end": v(-142, -1.58) * mm});
            skLineSegment(sketch, "E42.trimOffspring", {"start": v(-137.42, -47) * mm, "end": v(-75.58, -47) * mm});
            skLineSegment(sketch, "E43.trimOffspring", {"start": v(-142, 7.58) * mm, "end": v(-142, 42.42) * mm});
            skPoint(sketch, "E44.visualSharp", {"position": v(-139, 47) * mm});
            skArc(sketch, "E44.filletArc", {"start": v(-137.42, 47) * mm, "mid": v(-138.51, 46.67) * mm, "end": v(-139.25, 45.8) * mm});
            skPoint(sketch, "E45.visualSharp", {"position": v(-142, 44) * mm});
            skArc(sketch, "E45.filletArc", {"start": v(-140.8, 44.25) * mm, "mid": v(-141.67, 43.51) * mm, "end": v(-142, 42.42) * mm});
            skPoint(sketch, "E46.visualSharp", {"position": v(-69.83, 47) * mm});
            skArc(sketch, "E46.filletArc", {"start": v(-69.57, 45.8) * mm, "mid": v(-70.31, 46.67) * mm, "end": v(-71.4, 47) * mm});
            skPoint(sketch, "E47.visualSharp", {"position": v(-63.83, 47) * mm});
            skArc(sketch, "E47.filletArc", {"start": v(-62.24, 47) * mm, "mid": v(-63.34, 46.67) * mm, "end": v(-64.08, 45.8) * mm});
            skPoint(sketch, "E48.visualSharp", {"position": v(63.17, 47) * mm});
            skArc(sketch, "E48.filletArc", {"start": v(63.43, 45.8) * mm, "mid": v(62.69, 46.67) * mm, "end": v(61.6, 47) * mm});
            skPoint(sketch, "E49.visualSharp", {"position": v(69.17, 47) * mm});
            skArc(sketch, "E49.filletArc", {"start": v(70.76, 47) * mm, "mid": v(69.66, 46.67) * mm, "end": v(68.92, 45.8) * mm});
            skPoint(sketch, "E50.visualSharp", {"position": v(139, 47) * mm});
            skArc(sketch, "E50.filletArc", {"start": v(139.25, 45.8) * mm, "mid": v(138.51, 46.67) * mm, "end": v(137.42, 47) * mm});
            skPoint(sketch, "E51.visualSharp", {"position": v(142, 44) * mm});
            skArc(sketch, "E51.filletArc", {"start": v(142, 42.42) * mm, "mid": v(141.67, 43.51) * mm, "end": v(140.8, 44.25) * mm});
            skPoint(sketch, "E52.visualSharp", {"position": v(142, 6) * mm});
            skArc(sketch, "E52.filletArc", {"start": v(140.8, 5.75) * mm, "mid": v(141.67, 6.49) * mm, "end": v(142, 7.58) * mm});
            skPoint(sketch, "E53.visualSharp", {"position": v(142, 0) * mm});
            skArc(sketch, "E53.filletArc", {"start": v(142, -1.58) * mm, "mid": v(141.67, -0.49) * mm, "end": v(140.8, 0.25) * mm});
            skPoint(sketch, "E54.visualSharp", {"position": v(142, -44) * mm});
            skArc(sketch, "E54.filletArc", {"start": v(140.8, -44.25) * mm, "mid": v(141.67, -43.51) * mm, "end": v(142, -42.42) * mm});
            skPoint(sketch, "E55.visualSharp", {"position": v(139, -47) * mm});
            skArc(sketch, "E55.filletArc", {"start": v(137.42, -47) * mm, "mid": v(138.51, -46.67) * mm, "end": v(139.25, -45.8) * mm});
            skPoint(sketch, "E56.visualSharp", {"position": v(43, -47) * mm});
            skArc(sketch, "E56.filletArc", {"start": v(41.42, -47) * mm, "mid": v(42.51, -46.67) * mm, "end": v(43.25, -45.8) * mm});
            skPoint(sketch, "E57.visualSharp", {"position": v(49, -47) * mm});
            skArc(sketch, "E57.filletArc", {"start": v(48.75, -45.8) * mm, "mid": v(49.49, -46.67) * mm, "end": v(50.58, -47) * mm});
            skPoint(sketch, "E58.visualSharp", {"position": v(-74, -47) * mm});
            skArc(sketch, "E58.filletArc", {"start": v(-75.58, -47) * mm, "mid": v(-74.49, -46.67) * mm, "end": v(-73.75, -45.8) * mm});
            skPoint(sketch, "E59.visualSharp", {"position": v(-68, -47) * mm});
            skArc(sketch, "E59.filletArc", {"start": v(-68.25, -45.8) * mm, "mid": v(-67.51, -46.67) * mm, "end": v(-66.42, -47) * mm});
            skPoint(sketch, "E60.visualSharp", {"position": v(-142, -44) * mm});
            skArc(sketch, "E60.filletArc", {"start": v(-142, -42.42) * mm, "mid": v(-141.67, -43.51) * mm, "end": v(-140.8, -44.25) * mm});
            skPoint(sketch, "E61.visualSharp", {"position": v(-139, -47) * mm});
            skArc(sketch, "E61.filletArc", {"start": v(-139.25, -45.8) * mm, "mid": v(-138.51, -46.67) * mm, "end": v(-137.42, -47) * mm});
            skPoint(sketch, "E62.visualSharp", {"position": v(-142, 6) * mm});
            skArc(sketch, "E62.filletArc", {"start": v(-142, 7.58) * mm, "mid": v(-141.67, 6.49) * mm, "end": v(-140.8, 5.75) * mm});
            skPoint(sketch, "E63.visualSharp", {"position": v(-142, 0) * mm});
            skArc(sketch, "E63.filletArc", {"start": v(-140.8, 0.25) * mm, "mid": v(-141.67, -0.49) * mm, "end": v(-142, -1.58) * mm});
            skCircle(sketch, "E64", {"center": v(105.17, 47) * mm, "radius": 1.5 * mm});
            skArc(sketch, "E65", {"start": v(102.43, 45.8) * mm, "mid": v(105.17, 44) * mm, "end": v(107.92, 45.8) * mm});
            skLineSegment(sketch, "E66.trimOffspring", {"start": v(109.76, 47) * mm, "end": v(137.42, 47) * mm});
            skPoint(sketch, "E67.visualSharp", {"position": v(102.17, 47) * mm});
            skArc(sketch, "E67.filletArc", {"start": v(102.43, 45.8) * mm, "mid": v(101.69, 46.67) * mm, "end": v(100.6, 47) * mm});
            skPoint(sketch, "E68.visualSharp", {"position": v(108.17, 47) * mm});
            skArc(sketch, "E68.filletArc", {"start": v(109.76, 47) * mm, "mid": v(108.66, 46.67) * mm, "end": v(107.92, 45.8) * mm});
            skSolve(sketch);
        }
        {
            var Q0;
            Q0 = qSketchRegion(id + "F4", true);
            extrude(context, id + "F5", {"entities" : qUnion([Q0]), "operationType" : NewBodyOperationType.REMOVE, "endBound" : BoundingType.THROUGH_ALL, "oppositeDirection" : true, "depth" : 25 * mm});
        }
        {
            var Q0;
            Q0=makeQuery(id+"F1.opExtrude","CAP_FACE",FACE,{"disambiguationData":[OSD([sQuery(id+"F0.wireOp",EDGE,"E0.bottom"),sQuery(id+"F0.wireOp",EDGE,"E0.top"),sQuery(id+"F0.wireOp",EDGE,"E0.left"),sQuery(id+"F0.wireOp",EDGE,"E0.right"),sQuery(id+"F0.wireOp",EDGE,"E1.filletArc"),sQuery(id+"F0.wireOp",EDGE,"E2.filletArc"),sQuery(id+"F0.wireOp",EDGE,"E3.filletArc"),sQuery(id+"F0.wireOp",EDGE,"E4.filletArc")])],"isStart":false});
            var sketch = newSketch(context, id + "F6", { "sketchPlane" : qUnion([Q0])});
            skPoint(sketch, "E69.right.end.orphan", {"position": v(112, 37) * mm});
            skPoint(sketch, "E70.orphan", {"position": v(112, 19) * mm});
            skLineSegment(sketch, "E71.bottom", {"start": v(82.5, 51) * mm, "end": v(89.5, 51) * mm});
            skLineSegment(sketch, "E71.top", {"start": v(77, 47) * mm, "end": v(95, 47) * mm});
            skLineSegment(sketch, "E71.left", {"start": v(77, 49) * mm, "end": v(77, 47) * mm});
            skLineSegment(sketch, "E71.right", {"start": v(95, 49) * mm, "end": v(95, 47) * mm});
            skLineSegment(sketch, "E72.left", {"start": v(82.5, 51) * mm, "end": v(82.5, 49) * mm});
            skLineSegment(sketch, "E72.right", {"start": v(89.5, 51) * mm, "end": v(89.5, 49) * mm});
            skLineSegment(sketch, "E73.bottom", {"start": v(77, 49) * mm, "end": v(82.5, 49) * mm});
            skLineSegment(sketch, "E74.trimOffspring", {"start": v(89.5, 49) * mm, "end": v(95, 49) * mm});
            skPoint(sketch, "E75.orphan", {"position": v(77, 51) * mm});
            skSolve(sketch);
        }
        {
            var Q0;
            Q0 = qSketchRegion(id + "F6", true);
            extrude(context, id + "F7", {"entities" : qUnion([Q0]), "operationType" : NewBodyOperationType.REMOVE, "endBound" : BoundingType.THROUGH_ALL, "oppositeDirection" : true, "depth" : 25 * mm});
        }
    });
